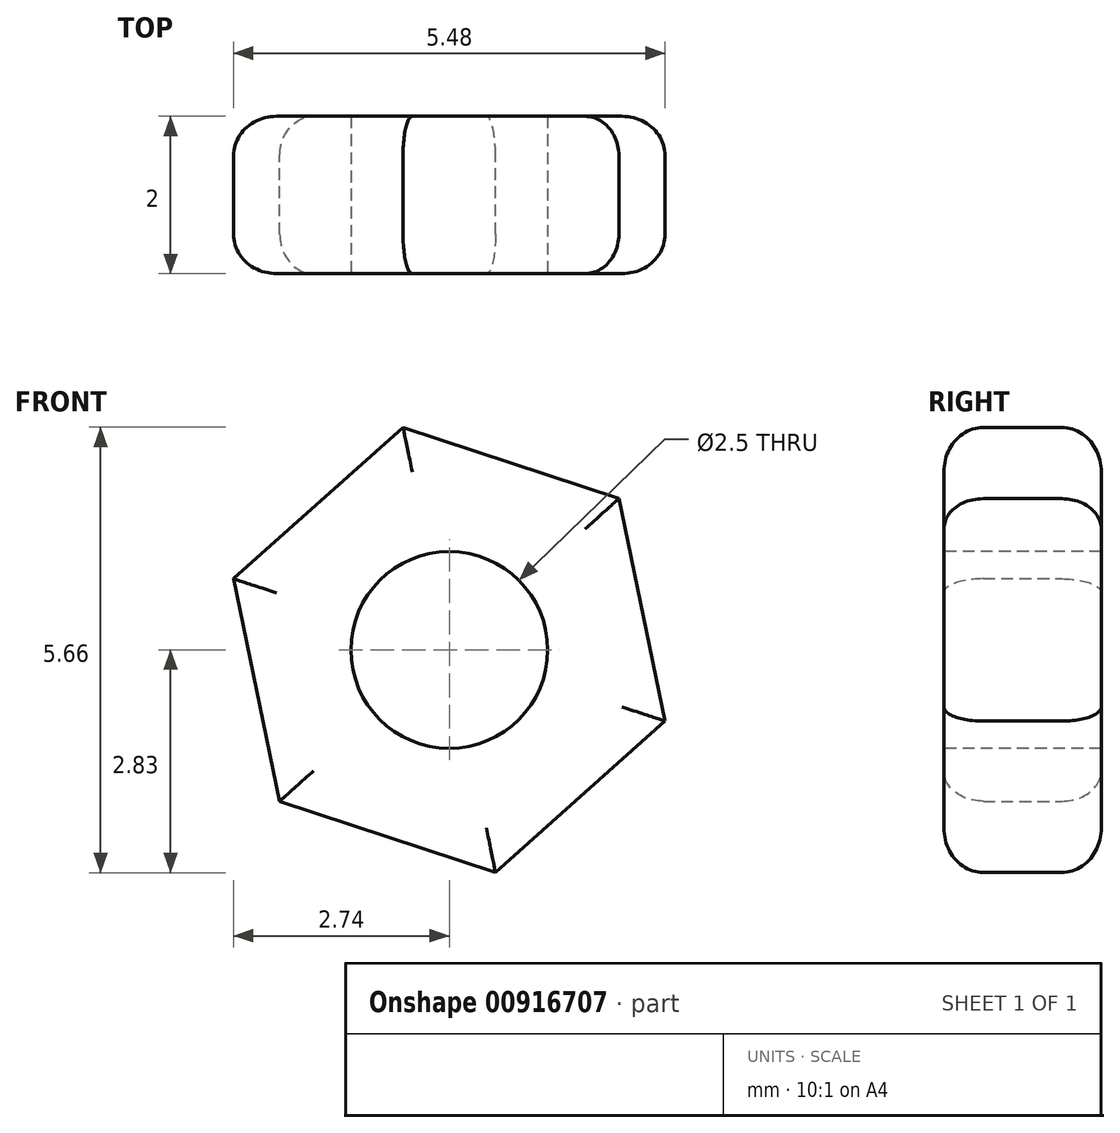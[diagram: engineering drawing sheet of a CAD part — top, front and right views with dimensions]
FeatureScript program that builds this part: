
annotation { "Feature Type Name" : "Feature", "Feature Type Description" : "" }
export const myFeature = defineFeature(function(context is Context, id is Id, definition is map)
    precondition{}
    {
        {
            var Q0;
            Q0=qCreatedBy(makeId("Front.planeOp"),FACE);
            var sketch = newSketch(context, id + "F0", { "sketchPlane" : qUnion([Q0])});
            skCircle(sketch, "E0.cCircle", {"center": v(0, 0) * mm, "radius": 2.5 * mm, "construction": true});
            skLineSegment(sketch, "E0.0", {"start": v(-2.74, 0.9) * mm, "end": v(-0.59, 2.83) * mm});
            skLineSegment(sketch, "E0.1", {"start": v(-0.59, 2.83) * mm, "end": v(2.15, 1.92) * mm});
            skLineSegment(sketch, "E0.2", {"start": v(2.15, 1.92) * mm, "end": v(2.74, -0.9) * mm});
            skLineSegment(sketch, "E0.3", {"start": v(2.74, -0.9) * mm, "end": v(0.59, -2.83) * mm});
            skLineSegment(sketch, "E0.4", {"start": v(0.59, -2.83) * mm, "end": v(-2.15, -1.92) * mm});
            skLineSegment(sketch, "E0.5", {"start": v(-2.15, -1.92) * mm, "end": v(-2.74, 0.9) * mm});
            skPoint(sketch, "E0.0.midPoint", {"position": v(-1.66, 1.87) * mm});
            skSolve(sketch);
        }
        {
            var Q0;
            Q0=qCreatedBy(makeId("Top.planeOp"),FACE);
            var sketch = newSketch(context, id + "F1", { "sketchPlane" : qUnion([Q0])});
            skLineSegment(sketch, "E1", {"start": v(0, 0) * mm, "end": v(0, 2) * mm});
            skSolve(sketch);
        }
        {
            var Q0;
            Q0 = qSketchRegion(id + "F0", true);
            var Q1;
            Q1 = qConstructionFilter(qBodyType(qCreatedBy(id + "F1" ,EDGE), BodyType.WIRE), ConstructionObject.NO);
            sweep(context, id + "F2", {"profiles" : qUnion([Q0]), "path" : qUnion([Q1])});
        }
        {
            var Q0;
            Q0=makeQuery(id+"F2.opSweep","CAP_EDGE",EDGE,{"disambiguationData":[OSD([sQuery(id+"F0.wireOp",EDGE,"E0.5"),sQuery(id+"F1.wireOp",VERTEX,"E1.start")])],"isStart":true});
            var Q1;
            Q1=makeQuery(id+"F2.opSweep","CAP_EDGE",EDGE,{"disambiguationData":[OSD([sQuery(id+"F0.wireOp",EDGE,"E0.0"),sQuery(id+"F1.wireOp",VERTEX,"E1.start")])],"isStart":true});
            var Q2;
            Q2=makeQuery(id+"F2.opSweep","CAP_EDGE",EDGE,{"disambiguationData":[OSD([sQuery(id+"F0.wireOp",EDGE,"E0.1"),sQuery(id+"F1.wireOp",VERTEX,"E1.start")])],"isStart":true});
            var Q3;
            Q3=makeQuery(id+"F2.opSweep","CAP_EDGE",EDGE,{"disambiguationData":[OSD([sQuery(id+"F0.wireOp",EDGE,"E0.2"),sQuery(id+"F1.wireOp",VERTEX,"E1.start")])],"isStart":true});
            var Q4;
            Q4=makeQuery(id+"F2.opSweep","CAP_EDGE",EDGE,{"disambiguationData":[OSD([sQuery(id+"F0.wireOp",EDGE,"E0.3"),sQuery(id+"F1.wireOp",VERTEX,"E1.start")])],"isStart":true});
            var Q5;
            Q5=makeQuery(id+"F2.opSweep","CAP_EDGE",EDGE,{"disambiguationData":[OSD([sQuery(id+"F0.wireOp",EDGE,"E0.4"),sQuery(id+"F1.wireOp",VERTEX,"E1.start")])],"isStart":true});
            var Q6;
            Q6=makeQuery(id+"F2.opSweep","CAP_EDGE",EDGE,{"disambiguationData":[OSD([sQuery(id+"F0.wireOp",EDGE,"E0.0"),sQuery(id+"F1.wireOp",VERTEX,"E1.end")])],"isStart":false});
            var Q7;
            Q7=makeQuery(id+"F2.opSweep","CAP_EDGE",EDGE,{"disambiguationData":[OSD([sQuery(id+"F0.wireOp",EDGE,"E0.1"),sQuery(id+"F1.wireOp",VERTEX,"E1.end")])],"isStart":false});
            var Q8;
            Q8=makeQuery(id+"F2.opSweep","CAP_EDGE",EDGE,{"disambiguationData":[OSD([sQuery(id+"F0.wireOp",EDGE,"E0.2"),sQuery(id+"F1.wireOp",VERTEX,"E1.end")])],"isStart":false});
            var Q9;
            Q9=makeQuery(id+"F2.opSweep","CAP_EDGE",EDGE,{"disambiguationData":[OSD([sQuery(id+"F0.wireOp",EDGE,"E0.3"),sQuery(id+"F1.wireOp",VERTEX,"E1.end")])],"isStart":false});
            var Q10;
            Q10=makeQuery(id+"F2.opSweep","CAP_EDGE",EDGE,{"disambiguationData":[OSD([sQuery(id+"F0.wireOp",EDGE,"E0.4"),sQuery(id+"F1.wireOp",VERTEX,"E1.end")])],"isStart":false});
            var Q11;
            Q11=makeQuery(id+"F2.opSweep","CAP_EDGE",EDGE,{"disambiguationData":[OSD([sQuery(id+"F0.wireOp",EDGE,"E0.5"),sQuery(id+"F1.wireOp",VERTEX,"E1.end")])],"isStart":false});
            fillet(context, id + "F3", {"entities" : qUnion([Q0, Q1, Q2, Q3, Q4, Q5, Q6, Q7, Q8, Q9, Q10, Q11]), "radius" : 0.5 * mm, "tangentPropagation" : true, "allowEdgeOverflow" : false});
        }
        {
            var Q0;
            Q0=qCreatedBy(makeId("Front.planeOp"),FACE);
            var sketch = newSketch(context, id + "F4", { "sketchPlane" : qUnion([Q0])});
            skCircle(sketch, "E2", {"center": v(0, 0) * mm, "radius": 1.25 * mm});
            skSolve(sketch);
        }
        {
            var Q0;
            Q0=qCreatedBy(makeId("Top.planeOp"),FACE);
            var sketch = newSketch(context, id + "F5", { "sketchPlane" : qUnion([Q0])});
            skLineSegment(sketch, "E3", {"start": v(0, -0.64) * mm, "end": v(0, 2.51) * mm});
            skSolve(sketch);
        }
        {
            var Q0;
            Q0 = qSketchRegion(id + "F4", true);
            var Q1;
            Q1 = qConstructionFilter(qBodyType(qCreatedBy(id + "F5" ,EDGE), BodyType.WIRE), ConstructionObject.NO);
            sweep(context, id + "F6", {"operationType" : NewBodyOperationType.REMOVE, "profiles" : qUnion([Q0]), "path" : qUnion([Q1])});
        }
    });
